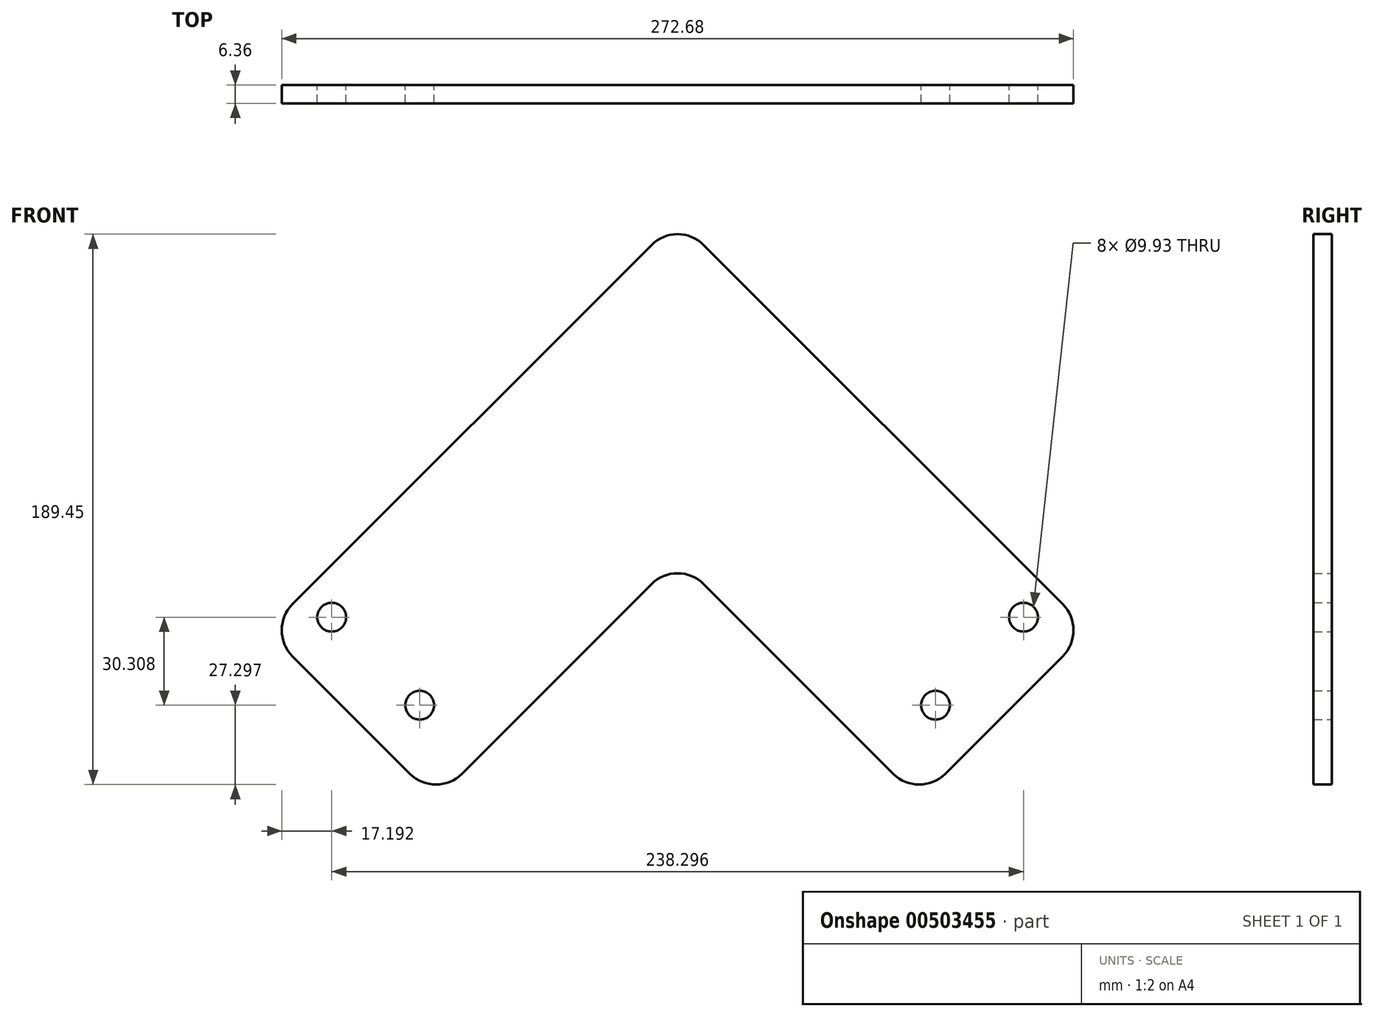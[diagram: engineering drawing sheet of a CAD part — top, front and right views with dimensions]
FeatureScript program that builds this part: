
annotation { "Feature Type Name" : "Feature", "Feature Type Description" : "" }
export const myFeature = defineFeature(function(context is Context, id is Id, definition is map)
    precondition{}
    {
        {
            var Q0;
            Q0=qCreatedBy(makeId("Front.planeOp"),FACE);
            var sketch = newSketch(context, id + "F0", { "sketchPlane" : qUnion([Q0])});
            skLineSegment(sketch, "E0", {"start": v(0, 0) * mm, "end": v(-83.23, -83.23) * mm});
            skLineSegment(sketch, "E1", {"start": v(0, 0) * mm, "end": v(0, 116.74) * mm});
            skLineSegment(sketch, "E2", {"start": v(-83.23, -83.23) * mm, "end": v(-141.6, -24.86) * mm});
            skLineSegment(sketch, "E3", {"start": v(-141.6, -24.86) * mm, "end": v(0, 116.74) * mm});
            skPoint(sketch, "E4", {"position": v(-15.88, 114.34) * mm});
            skPoint(sketch, "E5", {"position": v(-15.88, -29.35) * mm});
            skLineSegment(sketch, "E6.MirrorCS", {"start": v(0, 0) * mm, "end": v(83.23, -83.23) * mm});
            skPoint(sketch, "E7.MirrorP", {"position": v(15.88, -29.35) * mm});
            skLineSegment(sketch, "E8.MirrorCS", {"start": v(83.23, -83.23) * mm, "end": v(141.6, -24.86) * mm});
            skLineSegment(sketch, "E9.MirrorCS", {"start": v(141.6, -24.86) * mm, "end": v(0, 116.74) * mm});
            skPoint(sketch, "E10.MirrorP", {"position": v(15.88, 114.34) * mm});
            skLineSegment(sketch, "E11", {"start": v(-15.87, -29.35) * mm, "end": v(-69.76, 24.54) * mm, "construction": true});
            skLineSegment(sketch, "E12", {"start": v(-15.88, 114.34) * mm, "end": v(38, 60.46) * mm, "construction": true});
            skCircle(sketch, "E13", {"center": v(-88.84, -50.67) * mm, "radius": 4.97 * mm});
            skLineSegment(sketch, "E14", {"start": v(-88.84, -50.67) * mm, "end": v(-128.13, -11.38) * mm, "construction": true});
            skCircle(sketch, "E15", {"center": v(-119.15, -20.37) * mm, "radius": 4.97 * mm});
            skCircle(sketch, "E16.MirrorC", {"center": v(88.84, -50.67) * mm, "radius": 4.97 * mm});
            skCircle(sketch, "E17.MirrorC", {"center": v(119.15, -20.37) * mm, "radius": 4.97 * mm});
            skLineSegment(sketch, "E18", {"start": v(-37.2, 41.37) * mm, "end": v(2.09, 2.09) * mm});
            skPoint(sketch, "E19", {"position": v(-108.48, -31.03) * mm});
            skSolve(sketch);
        }
        {
            var Q0;
            Q0=qSketchRegion(id+"F0",true);
            extrude(context, id + "F1", {"entities" : qUnion([Q0]), "depth" : 6.35 * mm, "offsetDistance" : 25.4 * mm, "symmetric" : true});
        }
        {
            var Q0;
            Q0=makeQuery(id+"F1.opExtrude","SWEPT_EDGE",EDGE,{"disambiguationData":[OSD([sQuery(id+"F0.wireOp",EDGE,"E2"),sQuery(id+"F0.wireOp",EDGE,"E3")])]});
            var Q1;
            Q1=makeQuery(id+"F1.opExtrude","SWEPT_EDGE",EDGE,{"disambiguationData":[OSD([sQuery(id+"F0.wireOp",EDGE,"E3"),sQuery(id+"F0.wireOp",EDGE,"E1"),sQuery(id+"F0.wireOp",EDGE,"E9.MirrorCS")])]});
            var Q2;
            Q2=makeQuery(id+"F1.opExtrude","SWEPT_EDGE",EDGE,{"disambiguationData":[OSD([sQuery(id+"F0.wireOp",EDGE,"E0"),sQuery(id+"F0.wireOp",EDGE,"E6.MirrorCS"),sQuery(id+"F0.wireOp",EDGE,"E1")])]});
            var Q3;
            Q3=makeQuery(id+"F1.opExtrude","SWEPT_EDGE",EDGE,{"disambiguationData":[OSD([sQuery(id+"F0.wireOp",EDGE,"E6.MirrorCS"),sQuery(id+"F0.wireOp",EDGE,"E8.MirrorCS")])]});
            var Q4;
            Q4=makeQuery(id+"F1.opExtrude","SWEPT_EDGE",EDGE,{"disambiguationData":[OSD([sQuery(id+"F0.wireOp",EDGE,"E8.MirrorCS"),sQuery(id+"F0.wireOp",EDGE,"E9.MirrorCS")])]});
            var Q5;
            Q5=makeQuery(id+"F1.opExtrude","SWEPT_EDGE",EDGE,{"disambiguationData":[OSD([sQuery(id+"F0.wireOp",EDGE,"E0"),sQuery(id+"F0.wireOp",EDGE,"E2")])]});
            fillet(context, id + "F2", {"entities" : qUnion([Q0, Q1, Q2, Q3, Q4, Q5]), "radius" : 12.7 * mm, "tangentPropagation" : true, "allowEdgeOverflow" : false});
        }
    });
